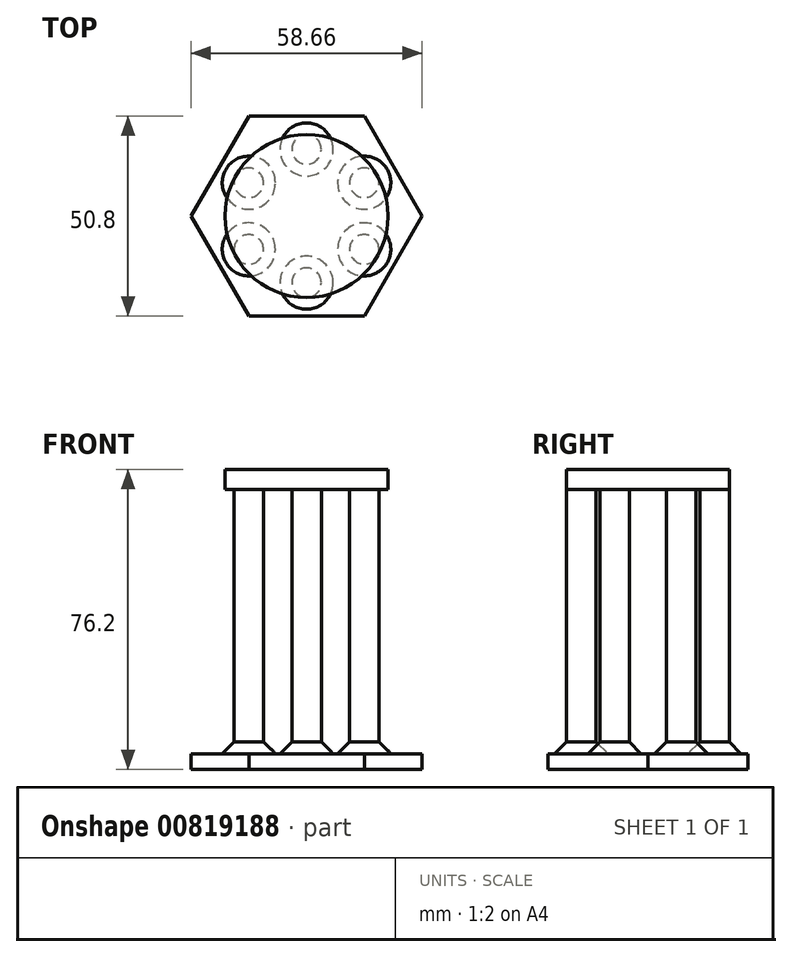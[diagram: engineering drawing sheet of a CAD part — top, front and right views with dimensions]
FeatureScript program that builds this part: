
annotation { "Feature Type Name" : "Feature", "Feature Type Description" : "" }
export const myFeature = defineFeature(function(context is Context, id is Id, definition is map)
    precondition{}
    {
        {
            var Q0;
            Q0=qCreatedBy(makeId("Top.planeOp"),FACE);
            var sketch = newSketch(context, id + "F0", { "sketchPlane" : qUnion([Q0])});
            skCircle(sketch, "E0.cCircle", {"center": v(0, 0) * mm, "radius": 25.4 * mm, "construction": true});
            skLineSegment(sketch, "E0.0", {"start": v(-14.66, 25.4) * mm, "end": v(14.66, 25.4) * mm});
            skLineSegment(sketch, "E0.1", {"start": v(14.66, 25.4) * mm, "end": v(29.33, 0) * mm});
            skLineSegment(sketch, "E0.2", {"start": v(29.33, 0) * mm, "end": v(14.66, -25.4) * mm});
            skLineSegment(sketch, "E0.3", {"start": v(14.66, -25.4) * mm, "end": v(-14.66, -25.4) * mm});
            skLineSegment(sketch, "E0.4", {"start": v(-14.66, -25.4) * mm, "end": v(-29.33, 0) * mm});
            skLineSegment(sketch, "E0.5", {"start": v(-29.33, 0) * mm, "end": v(-14.66, 25.4) * mm});
            skPoint(sketch, "E0.0.midPoint", {"position": v(0, 25.4) * mm});
            skCircle(sketch, "E1", {"center": v(-14.66, 8.47) * mm, "radius": 3.75 * mm});
            skCircle(sketch, "E2", {"center": v(0, 16.93) * mm, "radius": 3.75 * mm});
            skCircle(sketch, "E3", {"center": v(14.66, 8.47) * mm, "radius": 3.75 * mm});
            skCircle(sketch, "E4", {"center": v(14.66, -8.47) * mm, "radius": 3.75 * mm});
            skCircle(sketch, "E5", {"center": v(0, -16.93) * mm, "radius": 3.75 * mm});
            skCircle(sketch, "E6", {"center": v(-14.66, -8.47) * mm, "radius": 3.75 * mm});
            skCircle(sketch, "E7", {"center": v(0, 0) * mm, "radius": 20.68 * mm});
            skSolve(sketch);
        }
        {
            var Q0;
            Q0=makeQuery(id+"F0.imprint","IMPRINT",FACE,{"disambiguationData":[TD([[makeQuery(id+"F0.imprint","IMPRINT",EDGE,{"derivedFrom":sQuery(id+"F0.wireOp",EDGE,"E0.0")}),-1.0]])]});
            var Q1;
            Q1=makeQuery(id+"F0.imprint","IMPRINT",FACE,{"disambiguationData":[TD([[makeQuery(id+"F0.imprint","IMPRINT",EDGE,{"derivedFrom":sQuery(id+"F0.wireOp",EDGE,"E1")}),1.0]])]});
            var Q2;
            Q2=makeQuery(id+"F0.imprint","IMPRINT",FACE,{"disambiguationData":[TD([[makeQuery(id+"F0.imprint","IMPRINT",EDGE,{"derivedFrom":sQuery(id+"F0.wireOp",EDGE,"E2")}),1.0]])]});
            var Q3;
            Q3=makeQuery(id+"F0.imprint","IMPRINT",FACE,{"disambiguationData":[TD([[makeQuery(id+"F0.imprint","IMPRINT",EDGE,{"derivedFrom":sQuery(id+"F0.wireOp",EDGE,"E3")}),1.0]])]});
            var Q4;
            Q4=makeQuery(id+"F0.imprint","IMPRINT",FACE,{"disambiguationData":[TD([[makeQuery(id+"F0.imprint","IMPRINT",EDGE,{"derivedFrom":sQuery(id+"F0.wireOp",EDGE,"E4")}),1.0]])]});
            var Q5;
            Q5=makeQuery(id+"F0.imprint","IMPRINT",FACE,{"disambiguationData":[TD([[makeQuery(id+"F0.imprint","IMPRINT",EDGE,{"derivedFrom":sQuery(id+"F0.wireOp",EDGE,"E6")}),1.0]])]});
            var Q6;
            Q6=makeQuery(id+"F0.imprint","IMPRINT",FACE,{"disambiguationData":[TD([[makeQuery(id+"F0.imprint","IMPRINT",EDGE,{"derivedFrom":sQuery(id+"F0.wireOp",EDGE,"E5")}),1.0]])]});
            var Q7;
            {var subQ5=sQuery(id+"F0.wireOp",EDGE,"E1");Q7=makeQuery(id+"F0.imprint","IMPRINT",FACE,{"disambiguationData":[TD([[makeQuery(id+"F0.imprint","IMPRINT",EDGE,{"derivedFrom":subQ5}),-1.0]])]});}
            extrude(context, id + "F1", {"entities" : qUnion([Q0, Q1, Q2, Q3, Q4, Q5, Q6, Q7]), "depth" : 4 * mm, "offsetDistance" : 25.4 * mm});
        }
        {
            var Q0;
            Q0=makeQuery(id+"F0.imprint","IMPRINT",FACE,{"disambiguationData":[TD([[makeQuery(id+"F0.imprint","IMPRINT",EDGE,{"derivedFrom":sQuery(id+"F0.wireOp",EDGE,"E2")}),1.0]])]});
            var Q1;
            Q1=makeQuery(id+"F0.imprint","IMPRINT",FACE,{"disambiguationData":[TD([[makeQuery(id+"F0.imprint","IMPRINT",EDGE,{"derivedFrom":sQuery(id+"F0.wireOp",EDGE,"E1")}),1.0]])]});
            var Q2;
            Q2=makeQuery(id+"F0.imprint","IMPRINT",FACE,{"disambiguationData":[TD([[makeQuery(id+"F0.imprint","IMPRINT",EDGE,{"derivedFrom":sQuery(id+"F0.wireOp",EDGE,"E3")}),1.0]])]});
            var Q3;
            Q3=makeQuery(id+"F0.imprint","IMPRINT",FACE,{"disambiguationData":[TD([[makeQuery(id+"F0.imprint","IMPRINT",EDGE,{"derivedFrom":sQuery(id+"F0.wireOp",EDGE,"E4")}),1.0]])]});
            var Q4;
            Q4=makeQuery(id+"F0.imprint","IMPRINT",FACE,{"disambiguationData":[TD([[makeQuery(id+"F0.imprint","IMPRINT",EDGE,{"derivedFrom":sQuery(id+"F0.wireOp",EDGE,"E5")}),1.0]])]});
            var Q5;
            Q5=makeQuery(id+"F0.imprint","IMPRINT",FACE,{"disambiguationData":[TD([[makeQuery(id+"F0.imprint","IMPRINT",EDGE,{"derivedFrom":sQuery(id+"F0.wireOp",EDGE,"E6")}),1.0]])]});
            extrude(context, id + "F2", {"entities" : qUnion([Q0, Q1, Q2, Q3, Q4, Q5]), "operationType" : NewBodyOperationType.ADD, "depth" : 71.12 * mm, "offsetDistance" : 25.4 * mm});
        }
        {
            var Q0;
            Q0=makeQuery(id+"F0.imprint","IMPRINT",FACE,{"disambiguationData":[TD([[makeQuery(id+"F0.imprint","IMPRINT",EDGE,{"derivedFrom":sQuery(id+"F0.wireOp",EDGE,"E5")}),1.0]])]});
            var Q1;
            Q1=makeQuery(id+"F0.imprint","IMPRINT",FACE,{"disambiguationData":[TD([[makeQuery(id+"F0.imprint","IMPRINT",EDGE,{"derivedFrom":sQuery(id+"F0.wireOp",EDGE,"E4")}),1.0]])]});
            var Q2;
            Q2=makeQuery(id+"F0.imprint","IMPRINT",FACE,{"disambiguationData":[TD([[makeQuery(id+"F0.imprint","IMPRINT",EDGE,{"derivedFrom":sQuery(id+"F0.wireOp",EDGE,"E3")}),1.0]])]});
            var Q3;
            Q3=makeQuery(id+"F0.imprint","IMPRINT",FACE,{"disambiguationData":[TD([[makeQuery(id+"F0.imprint","IMPRINT",EDGE,{"derivedFrom":sQuery(id+"F0.wireOp",EDGE,"E6")}),1.0]])]});
            var Q4;
            Q4=makeQuery(id+"F0.imprint","IMPRINT",FACE,{"disambiguationData":[TD([[makeQuery(id+"F0.imprint","IMPRINT",EDGE,{"derivedFrom":sQuery(id+"F0.wireOp",EDGE,"E1")}),1.0]])]});
            var Q5;
            Q5=makeQuery(id+"F0.imprint","IMPRINT",FACE,{"disambiguationData":[TD([[makeQuery(id+"F0.imprint","IMPRINT",EDGE,{"derivedFrom":sQuery(id+"F0.wireOp",EDGE,"E2")}),1.0]])]});
            var Q6;
            {var subQ5=sQuery(id+"F0.wireOp",EDGE,"E1");Q6=makeQuery(id+"F0.imprint","IMPRINT",FACE,{"disambiguationData":[TD([[makeQuery(id+"F0.imprint","IMPRINT",EDGE,{"derivedFrom":subQ5}),-1.0]])]});}
            extrude(context, id + "F3", {"entities" : qUnion([Q0, Q1, Q2, Q3, Q4, Q5, Q6]), "depth" : 76.2 * mm, "offsetDistance" : 25.4 * mm, "hasSecondDirection" : true, "secondDirectionOppositeDirection" : false, "secondDirectionDepth" : 71.12 * mm});
        }
        {
            var Q0;
            Q0=makeQuery(id+"F2.boolean.opBoolean","INTERSECT",EDGE,{"derivedFrom":[makeQuery(id+"F1.opExtrude","CAP_FACE",FACE,{"disambiguationData":[OSD([sQuery(id+"F0.wireOp",EDGE,"E0.0"),sQuery(id+"F0.wireOp",EDGE,"E0.1"),sQuery(id+"F0.wireOp",EDGE,"E0.2"),sQuery(id+"F0.wireOp",EDGE,"E0.3"),sQuery(id+"F0.wireOp",EDGE,"E0.4"),sQuery(id+"F0.wireOp",EDGE,"E0.5")])],"isStart":false}),makeQuery(id+"F2.opExtrude","SWEPT_FACE",FACE,{"disambiguationData":[OSD([sQuery(id+"F0.wireOp",EDGE,"E4")])]})]});
            var Q1;
            Q1=makeQuery(id+"F2.boolean.opBoolean","INTERSECT",EDGE,{"derivedFrom":[makeQuery(id+"F1.opExtrude","CAP_FACE",FACE,{"disambiguationData":[OSD([sQuery(id+"F0.wireOp",EDGE,"E0.0"),sQuery(id+"F0.wireOp",EDGE,"E0.1"),sQuery(id+"F0.wireOp",EDGE,"E0.2"),sQuery(id+"F0.wireOp",EDGE,"E0.3"),sQuery(id+"F0.wireOp",EDGE,"E0.4"),sQuery(id+"F0.wireOp",EDGE,"E0.5")])],"isStart":false}),makeQuery(id+"F2.opExtrude","SWEPT_FACE",FACE,{"disambiguationData":[OSD([sQuery(id+"F0.wireOp",EDGE,"E5")])]})]});
            var Q2;
            Q2=makeQuery(id+"F2.boolean.opBoolean","INTERSECT",EDGE,{"derivedFrom":[makeQuery(id+"F1.opExtrude","CAP_FACE",FACE,{"disambiguationData":[OSD([sQuery(id+"F0.wireOp",EDGE,"E0.0"),sQuery(id+"F0.wireOp",EDGE,"E0.1"),sQuery(id+"F0.wireOp",EDGE,"E0.2"),sQuery(id+"F0.wireOp",EDGE,"E0.3"),sQuery(id+"F0.wireOp",EDGE,"E0.4"),sQuery(id+"F0.wireOp",EDGE,"E0.5")])],"isStart":false}),makeQuery(id+"F2.opExtrude","SWEPT_FACE",FACE,{"disambiguationData":[OSD([sQuery(id+"F0.wireOp",EDGE,"E3")])]})]});
            var Q3;
            Q3=makeQuery(id+"F2.boolean.opBoolean","INTERSECT",EDGE,{"derivedFrom":[makeQuery(id+"F1.opExtrude","CAP_FACE",FACE,{"disambiguationData":[OSD([sQuery(id+"F0.wireOp",EDGE,"E0.0"),sQuery(id+"F0.wireOp",EDGE,"E0.1"),sQuery(id+"F0.wireOp",EDGE,"E0.2"),sQuery(id+"F0.wireOp",EDGE,"E0.3"),sQuery(id+"F0.wireOp",EDGE,"E0.4"),sQuery(id+"F0.wireOp",EDGE,"E0.5")])],"isStart":false}),makeQuery(id+"F2.opExtrude","SWEPT_FACE",FACE,{"disambiguationData":[OSD([sQuery(id+"F0.wireOp",EDGE,"E2")])]})]});
            var Q4;
            Q4=makeQuery(id+"F2.boolean.opBoolean","INTERSECT",EDGE,{"derivedFrom":[makeQuery(id+"F1.opExtrude","CAP_FACE",FACE,{"disambiguationData":[OSD([sQuery(id+"F0.wireOp",EDGE,"E0.0"),sQuery(id+"F0.wireOp",EDGE,"E0.1"),sQuery(id+"F0.wireOp",EDGE,"E0.2"),sQuery(id+"F0.wireOp",EDGE,"E0.3"),sQuery(id+"F0.wireOp",EDGE,"E0.4"),sQuery(id+"F0.wireOp",EDGE,"E0.5")])],"isStart":false}),makeQuery(id+"F2.opExtrude","SWEPT_FACE",FACE,{"disambiguationData":[OSD([sQuery(id+"F0.wireOp",EDGE,"E1")])]})]});
            var Q5;
            Q5=makeQuery(id+"F2.boolean.opBoolean","INTERSECT",EDGE,{"derivedFrom":[makeQuery(id+"F1.opExtrude","CAP_FACE",FACE,{"disambiguationData":[OSD([sQuery(id+"F0.wireOp",EDGE,"E0.0"),sQuery(id+"F0.wireOp",EDGE,"E0.1"),sQuery(id+"F0.wireOp",EDGE,"E0.2"),sQuery(id+"F0.wireOp",EDGE,"E0.3"),sQuery(id+"F0.wireOp",EDGE,"E0.4"),sQuery(id+"F0.wireOp",EDGE,"E0.5")])],"isStart":false}),makeQuery(id+"F2.opExtrude","SWEPT_FACE",FACE,{"disambiguationData":[OSD([sQuery(id+"F0.wireOp",EDGE,"E6")])]})]});
            chamfer(context, id + "F4", {"entities" : qUnion([Q0, Q1, Q2, Q3, Q4, Q5]), "width" : 3 * mm, "tangentPropagation" : true});
        }
    });
